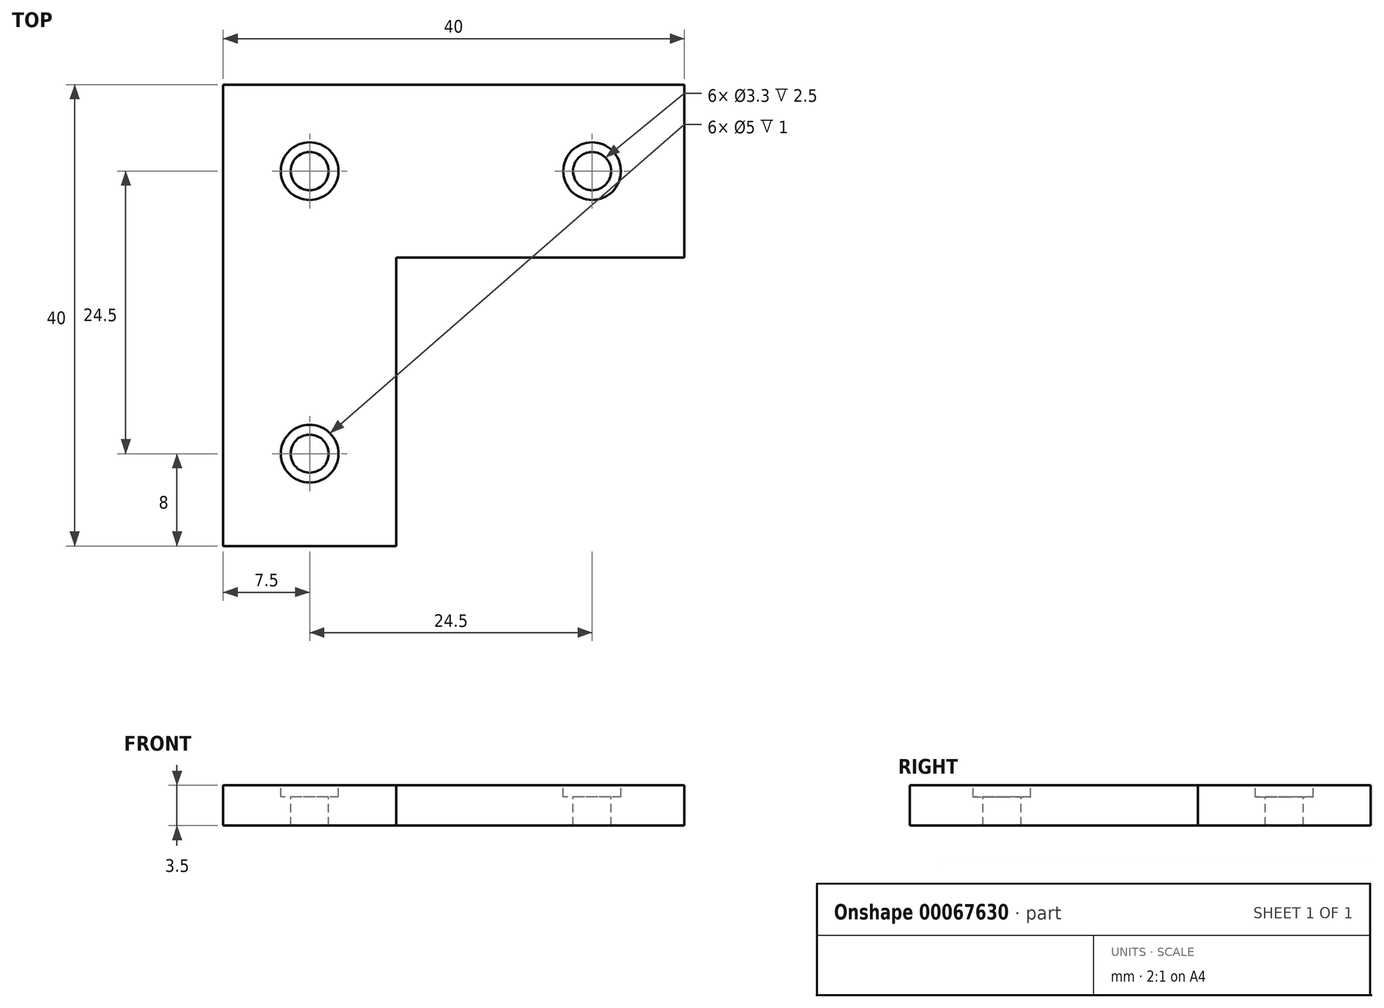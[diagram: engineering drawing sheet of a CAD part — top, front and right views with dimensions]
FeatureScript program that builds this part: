
annotation { "Feature Type Name" : "Feature", "Feature Type Description" : "" }
export const myFeature = defineFeature(function(context is Context, id is Id, definition is map)
    precondition{}
    {
        {
            var Q0;
            Q0=qCreatedBy(makeId("Top.planeOp"),FACE);
            var sketch = newSketch(context, id + "F0", { "sketchPlane" : qUnion([Q0])});
            skLineSegment(sketch, "E0.rect.bottom", {"start": v(-7.5, 20) * mm, "end": v(7.5, 20) * mm});
            skLineSegment(sketch, "E0.rect.top", {"start": v(-7.5, -20) * mm, "end": v(7.5, -20) * mm});
            skLineSegment(sketch, "E0.rect.left", {"start": v(-7.5, 20) * mm, "end": v(-7.5, -20) * mm});
            skLineSegment(sketch, "E0.rect.right", {"start": v(7.5, 20) * mm, "end": v(7.5, -20) * mm});
            skPoint(sketch, "E0.rect.middle", {"position": v(0, 0) * mm});
            skLineSegment(sketch, "E1.bottom", {"start": v(7.5, 20) * mm, "end": v(32.5, 20) * mm});
            skLineSegment(sketch, "E1.top", {"start": v(7.5, 5) * mm, "end": v(32.5, 5) * mm});
            skLineSegment(sketch, "E1.left", {"start": v(7.5, 20) * mm, "end": v(7.5, 5) * mm});
            skLineSegment(sketch, "E1.right", {"start": v(32.5, 20) * mm, "end": v(32.5, 5) * mm});
            skSolve(sketch);
        }
        {
            var Q0;
            Q0=makeQuery(id+"F0.imprint","IMPRINT",FACE,{"disambiguationData":[TD([[makeQuery(id+"F0.imprint","IMPRINT",EDGE,{"derivedFrom":sQuery(id+"F0.wireOp",EDGE,"E0.rect.bottom")}),-1.0]])]});
            var Q1;
            Q1=makeQuery(id+"F0.imprint","IMPRINT",FACE,{"disambiguationData":[TD([[makeQuery(id+"F0.imprint","IMPRINT",EDGE,{"derivedFrom":sQuery(id+"F0.wireOp",EDGE,"E1.bottom")}),-1.0]])]});
            extrude(context, id + "F1", {"entities" : qUnion([Q0, Q1]), "depth" : 3.5 * mm});
        }
        {
            var Q0;
            Q0=makeQuery(id+"F1.opExtrude","CAP_FACE",FACE,{"disambiguationData":[OSD([sQuery(id+"F0.wireOp",EDGE,"E0.rect.bottom"),sQuery(id+"F0.wireOp",EDGE,"E0.rect.top"),sQuery(id+"F0.wireOp",EDGE,"E0.rect.left"),sQuery(id+"F0.wireOp",EDGE,"E0.rect.right"),sQuery(id+"F0.wireOp",EDGE,"E1.bottom"),sQuery(id+"F0.wireOp",EDGE,"E1.top"),sQuery(id+"F0.wireOp",EDGE,"E1.right")])],"isStart":false});
            var sketch = newSketch(context, id + "F2", { "sketchPlane" : qUnion([Q0])});
            skCircle(sketch, "E2", {"center": v(0, -12) * mm, "radius": 1.65 * mm});
            skCircle(sketch, "E3", {"center": v(24.5, 12.5) * mm, "radius": 1.65 * mm});
            skCircle(sketch, "E4", {"center": v(0, 12.5) * mm, "radius": 1.65 * mm});
            skCircle(sketch, "E5", {"center": v(0, -12) * mm, "radius": 2.5 * mm});
            skCircle(sketch, "E6", {"center": v(24.5, 12.5) * mm, "radius": 2.5 * mm});
            skCircle(sketch, "E7", {"center": v(0, 12.5) * mm, "radius": 2.5 * mm});
            skSolve(sketch);
        }
        {
            var Q0;
            Q0=makeQuery(id+"F2.imprint","IMPRINT",FACE,{"disambiguationData":[TD([[makeQuery(id+"F2.imprint","IMPRINT",EDGE,{"derivedFrom":sQuery(id+"F2.wireOp",EDGE,"E4")}),1.0]])]});
            var Q1;
            Q1=makeQuery(id+"F2.imprint","IMPRINT",FACE,{"disambiguationData":[TD([[makeQuery(id+"F2.imprint","IMPRINT",EDGE,{"derivedFrom":sQuery(id+"F2.wireOp",EDGE,"E2")}),1.0]])]});
            var Q2;
            Q2=makeQuery(id+"F2.imprint","IMPRINT",FACE,{"disambiguationData":[TD([[makeQuery(id+"F2.imprint","IMPRINT",EDGE,{"derivedFrom":sQuery(id+"F2.wireOp",EDGE,"E3")}),1.0]])]});
            extrude(context, id + "F3", {"entities" : qUnion([Q0, Q1, Q2]), "operationType" : NewBodyOperationType.REMOVE, "endBound" : BoundingType.UP_TO_NEXT, "oppositeDirection" : true, "depth" : 25 * mm});
        }
        {
            var Q0;
            Q0=makeQuery(id+"F2.imprint","IMPRINT",FACE,{"disambiguationData":[TD([[makeQuery(id+"F2.imprint","IMPRINT",EDGE,{"derivedFrom":sQuery(id+"F2.wireOp",EDGE,"E2")}),-1.0]])]});
            var Q1;
            Q1=makeQuery(id+"F2.imprint","IMPRINT",FACE,{"disambiguationData":[TD([[makeQuery(id+"F2.imprint","IMPRINT",EDGE,{"derivedFrom":sQuery(id+"F2.wireOp",EDGE,"E4")}),-1.0]])]});
            var Q2;
            Q2=makeQuery(id+"F2.imprint","IMPRINT",FACE,{"disambiguationData":[TD([[makeQuery(id+"F2.imprint","IMPRINT",EDGE,{"derivedFrom":sQuery(id+"F2.wireOp",EDGE,"E3")}),-1.0]])]});
            extrude(context, id + "F4", {"entities" : qUnion([Q0, Q1, Q2]), "operationType" : NewBodyOperationType.REMOVE, "oppositeDirection" : true, "depth" : 1 * mm});
        }
    });
